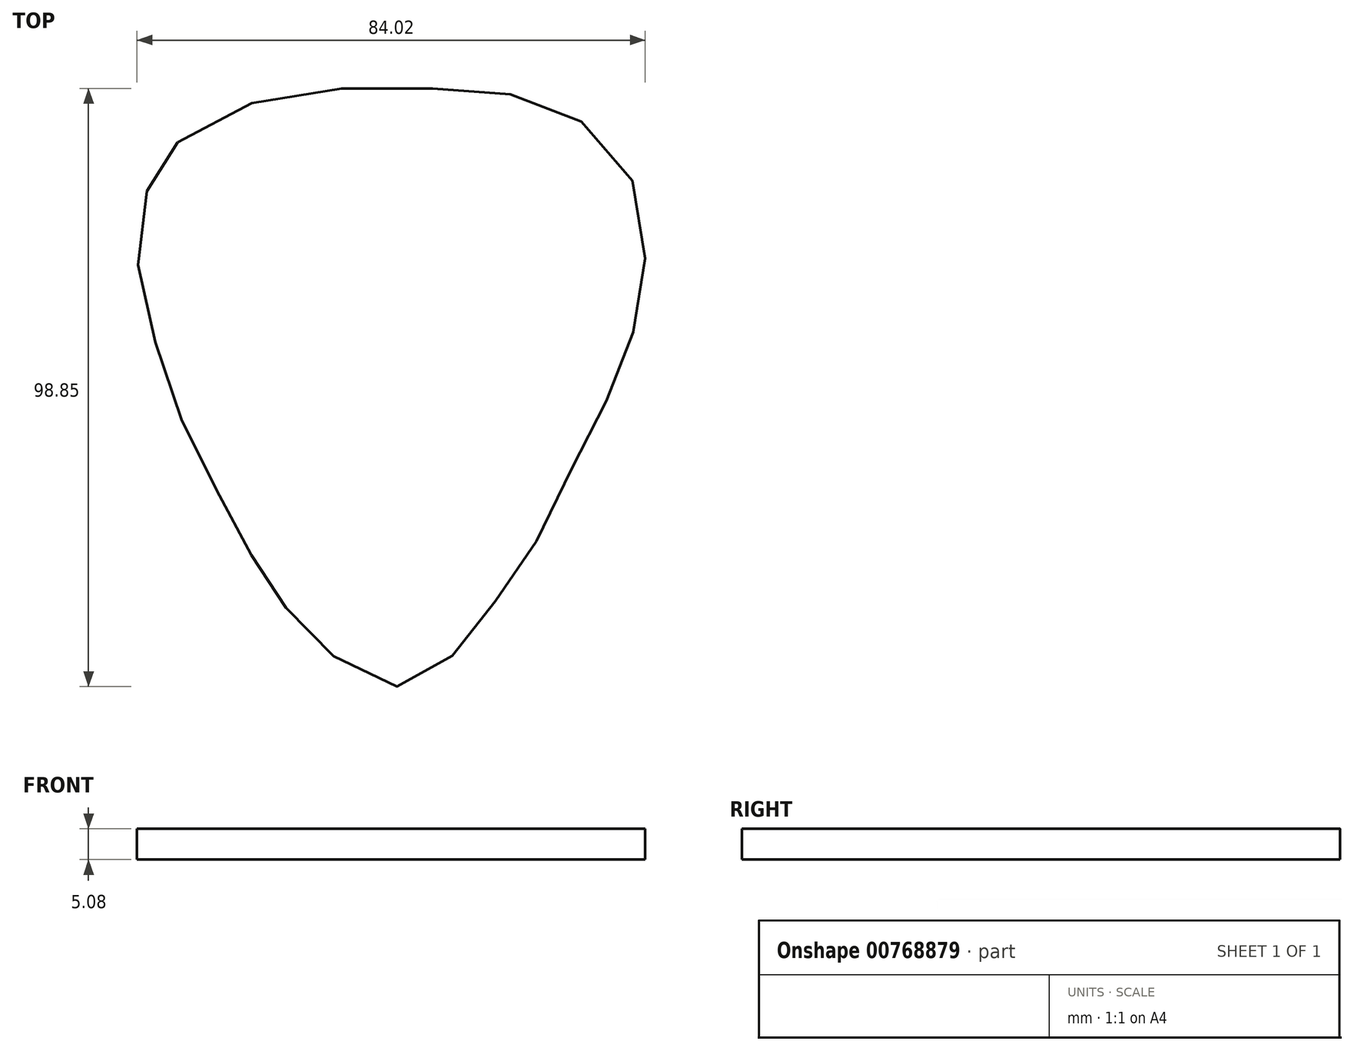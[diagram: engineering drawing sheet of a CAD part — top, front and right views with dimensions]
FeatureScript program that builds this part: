
annotation { "Feature Type Name" : "Feature", "Feature Type Description" : "" }
export const myFeature = defineFeature(function(context is Context, id is Id, definition is map)
    precondition{}
    {
        {
            var Q0;
            Q0=qCreatedBy(makeId("Top.planeOp"),FACE);
            var sketch = newSketch(context, id + "F0", { "sketchPlane" : qUnion([Q0])});
            skFitSpline(sketch, "E0", {"points": [v(-38.33, 30.7) * mm, v(-29.47, 35.88) * mm, v(-17.25, 39.24) * mm, v(-3.82, 39.55) * mm, v(7.79, 39.55) * mm, v(16.64, 38.63) * mm, v(25.2, 35.88) * mm, v(32.52, 30.7) * mm, v(37.71, 22.14) * mm, v(38.94, 12.67) * mm, v(38.33, 3.51) * mm, v(35.58, -4.12) * mm, v(32.52, -12.06) * mm, v(28.25, -20.3) * mm, v(24.28, -28.55) * mm, v(19.7, -37.4) * mm, v(15.12, -43.82) * mm, v(10.54, -50.24) * mm, v(5.65, -55.43) * mm, v(0, -59.1) * mm, v(-5.65, -58.18) * mm, v(-12.98, -53.9) * mm, v(-18.17, -48.7) * mm, v(-22.45, -43.82) * mm, v(-25.5, -38.63) * mm, v(-29.16, -32.22) * mm, v(-33.44, -23.67) * mm, v(-37.71, -15.12) * mm, v(-41.07, -5.34) * mm, v(-43.82, 3.82) * mm, v(-45.04, 13.59) * mm, v(-43.82, 21.83) * mm, v(-40.16, 27.64) * mm, v(-38.33, 30.7) * mm]});
            skSolve(sketch);
        }
        {
            var Q0;
            Q0 = qSketchRegion(id + "F0", true);
            extrude(context, id + "F1", {"entities" : qUnion([Q0]), "depth" : 5.08 * mm, "offsetDistance" : 25.4 * mm});
        }
    });
